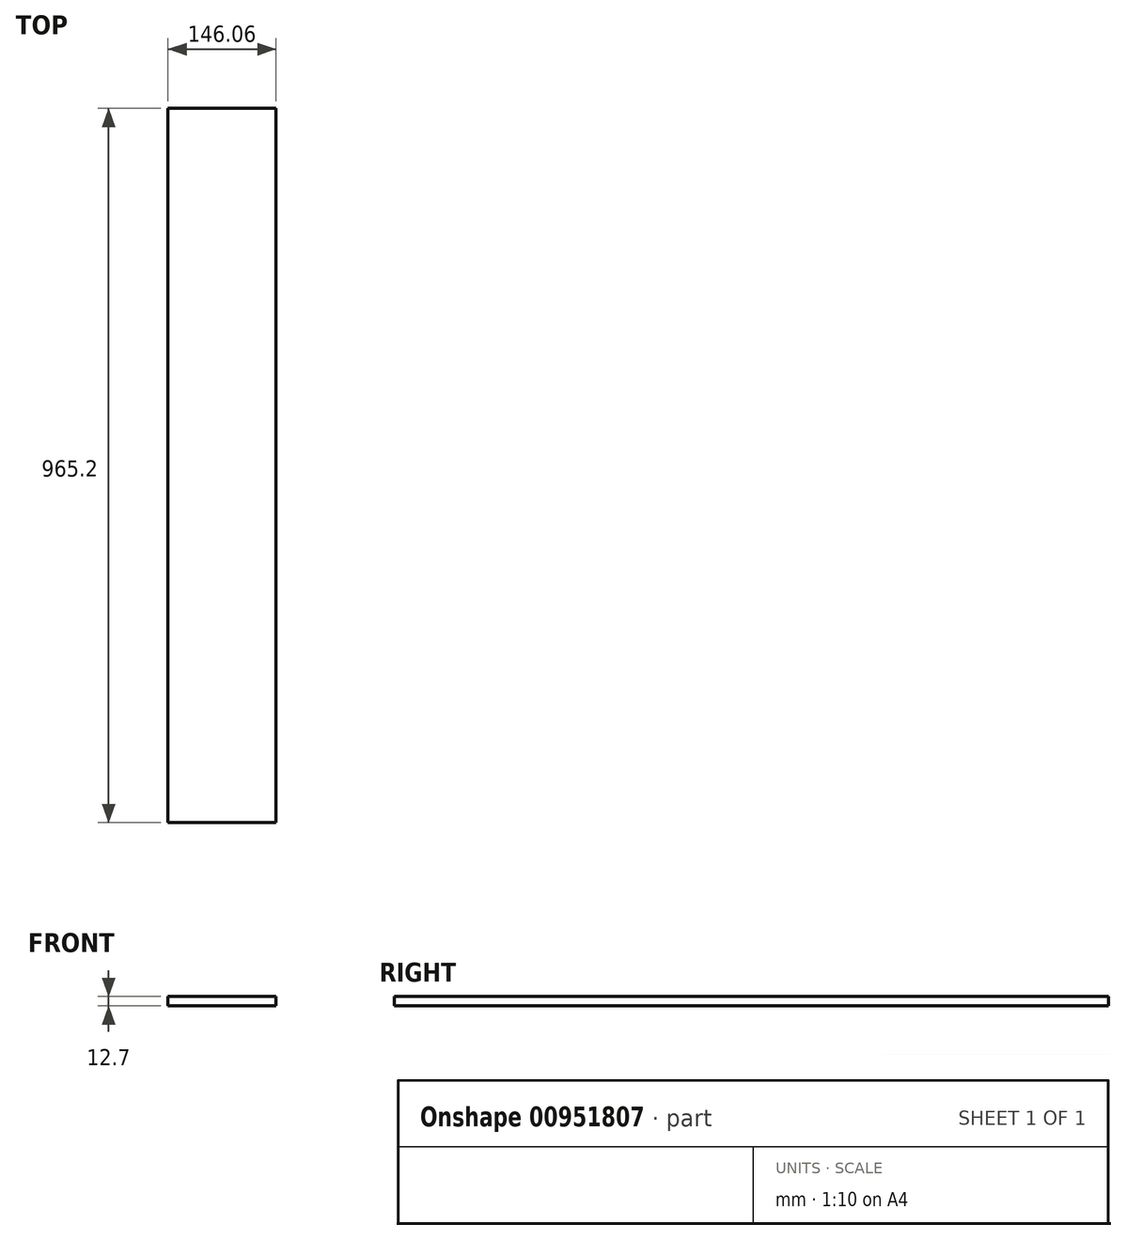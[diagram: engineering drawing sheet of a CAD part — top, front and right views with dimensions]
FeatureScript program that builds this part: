
annotation { "Feature Type Name" : "Feature", "Feature Type Description" : "" }
export const myFeature = defineFeature(function(context is Context, id is Id, definition is map)
    precondition{}
    {
        {
            var Q0;
            Q0=qCreatedBy(makeId("Top.planeOp"),FACE);
            var sketch = newSketch(context, id + "F0", { "sketchPlane" : qUnion([Q0])});
            skLineSegment(sketch, "E0.bottom", {"start": v(73.03, -482.6) * mm, "end": v(-73.02, -482.6) * mm});
            skLineSegment(sketch, "E0.top", {"start": v(73.02, 482.6) * mm, "end": v(-73.03, 482.6) * mm});
            skLineSegment(sketch, "E0.left", {"start": v(73.03, -482.6) * mm, "end": v(73.02, 482.6) * mm});
            skLineSegment(sketch, "E0.right", {"start": v(-73.02, -482.6) * mm, "end": v(-73.03, 482.6) * mm});
            skPoint(sketch, "E0.middle", {"position": v(0, 0) * mm});
            skSolve(sketch);
        }
        {
            var Q0;
            Q0 = qSketchRegion(id + "F0", true);
            extrude(context, id + "F1", {"entities" : qUnion([Q0]), "depth" : 12.7 * mm, "offsetDistance" : 25.4 * mm});
        }
    });
